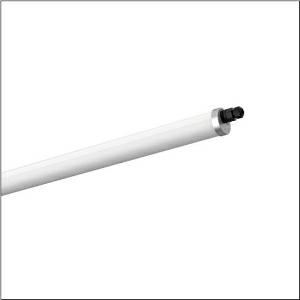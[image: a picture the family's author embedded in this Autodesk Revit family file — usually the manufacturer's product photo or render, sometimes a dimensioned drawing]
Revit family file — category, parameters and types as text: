
# Revit family: monsun_r__31_tube_51ft10dn460a_a449
name_source: partatom
category: Lighting Fixtures
units: mm (PartAtom-declared; Revit-internal decimal feet)

## family parameters
Cut with Voids When Loaded = No
Host = Face
Light Source = No
Part Type = Normal
Room Calculation Point = No
Round Connector Dimension = Use Diameter
Shared = No

## types (1)
- Monsun® 31 Tube (1 x LED, 6500 lm, 40 W, 4000K)
    Apparent Load = 40 VA
    CIE Flux Codes = 42 71 90 91 100
    Color Rendering = 80
    Color Temperature = 4000K
    Default Elevation = 1800 mm
    Description = Monsun® 31 Tube, tubular luminaire, primary optical cover: diffuser, of PMMA, light emission: direct distribution, primary light characteristic: symmetric, installation type: suspended mounting, surface-mounted, LED, rated luminous flux: 6.500lm, luminous efficacy: 160lm/W, light colour: 840, colour temperature: 4000K, control gear: DALI 2, with with 1 terminal, 5-pole, max. 2.5mm², through-wiring: 5x 1.5mm², mains connection: 220..240V, AC, 50/60Hz, rated input power: 40W, housing, cylindrical, of PMMA, semi-transparent, matt white, with luminaire and ceiling fastening, V4A, mounting with brackets of stainless steel, length: 1.570mm, diameter: 75mm, end cap, of stainless steel (V4A), protection rating (complete): IP67/IP69K, insulation class (complete): insulation class I (protective earthing), certification: CE, UKCA, impact resistance: IK07, permissible operating ambient temperature: -20..+40°C, corresponds to IFS (International Featured Standards) requirements for safety and quality in the food industry, usage in unprotected outdoor areas possible with horizontal mounting, contact your sales advisor before using the luminaires in applications with unclear chemical exposure, large temperature fluctuations or condensation-forming humidity, packaging unit: 1 piece
    Height = 83 mm
    Lamp = 1 x LED
    Lamp Light Flux = 6500 lm
    Lamp Power = 40 W
    Lamp count = 1
    Length = 1570 mm
    Luminous efficacy = 163 lm/W
    Manufacturer = Siteco
    ModVariant = No
    Model = 51FT10DN460A
    Mounting Place = Ceiling
    Mounting Type = Pendant
    Number of Poles = 1
    OnlyDefault = Yes
    Power Factor = 1
    Product Name = Monsun® 31 Tube
    Product group = tubular luminaire
    ProductGroupID = 906
    Protection Class = Protection class I
    RLX_Detail_Level = 1
    RLX_Emergency_Light_Flux = 0 lm
    RLX_Emergency_Type = 0
    RLX_Emergency_Type_DB = No
    RlxData = <blob elided: 25361 chars, md5=a5bb20ec>
    Socket = socket
    Standby Power = 0 W
    System Light Flux = 6500 lm
    System Power = 40 W
    Type Comments = Product without accessories
    Type Image = l_1228461.jpg
    URL = http://relux.com
    VarID = ---
    Voltage = 0 V
    Weight = 0.00 kg
    Width = 75 mm

## geometry (parser evidence)
native form markers: Blend x4, Sweep x13
no freeform markers — native parametric forms only
